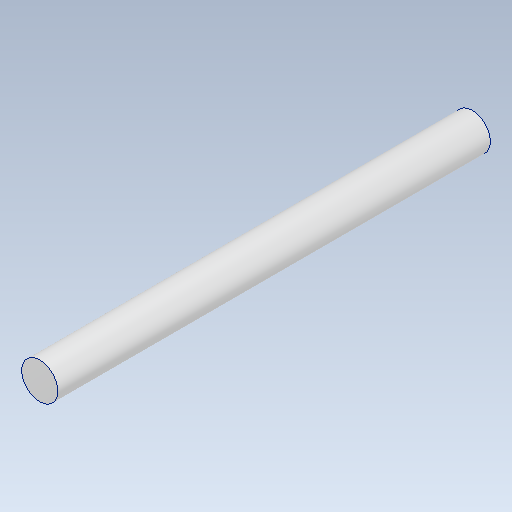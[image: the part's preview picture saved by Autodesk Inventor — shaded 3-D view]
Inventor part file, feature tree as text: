
AUTODESK INVENTOR PART (.ipt)
format: ipt  version: 2020.3 (Build 243373000, 373)  size: 97,280 bytes
history: native  units: mm
features: other x1, extrude x1, sketch x1
ambient origin geometry x8: Origin, YZ Plane, XZ Plane, XY Plane, X Axis, Y Axis, Z Axis, Center Point
bodies: Body1 (feature_tree)
feature tree (3):
  other  "ソリッド1"
  extrude  "押し出し1"  Depth=4.0mm
  sketch  "スケッチ1"
